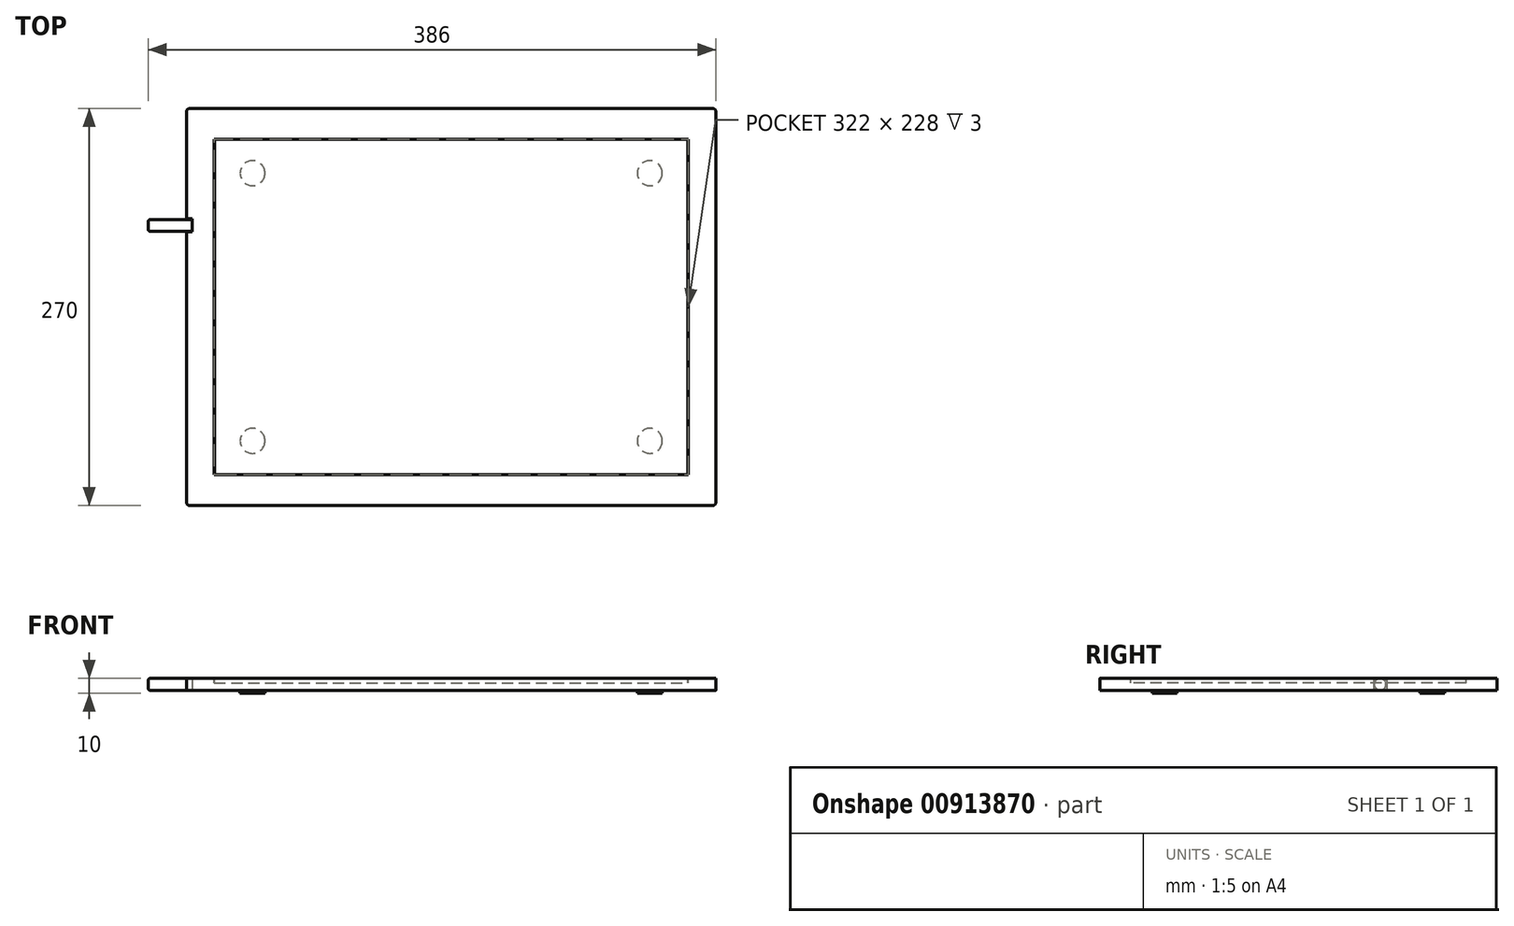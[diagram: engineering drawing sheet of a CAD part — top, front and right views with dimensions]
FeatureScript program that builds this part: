
annotation { "Feature Type Name" : "Feature", "Feature Type Description" : "" }
export const myFeature = defineFeature(function(context is Context, id is Id, definition is map)
    precondition{}
    {
        {
            var Q0;
            Q0=qCreatedBy(makeId("Top.planeOp"),FACE);
            var sketch = newSketch(context, id + "F0", { "sketchPlane" : qUnion([Q0])});
            skLineSegment(sketch, "E0.bottom", {"start": v(0, 0) * mm, "end": v(360, 0) * mm});
            skLineSegment(sketch, "E0.top", {"start": v(0, -270) * mm, "end": v(360, -270) * mm});
            skLineSegment(sketch, "E0.left", {"start": v(0, 0) * mm, "end": v(0, -270) * mm});
            skLineSegment(sketch, "E0.right", {"start": v(360, 0) * mm, "end": v(360, -270) * mm});
            skSolve(sketch);
        }
        {
            var Q0;
            Q0 = qSketchRegion(id + "F0", true);
            extrude(context, id + "F1", {"entities" : qUnion([Q0]), "depth" : 8 * mm, "offsetDistance" : 25 * mm});
        }
        {
            var Q0;
            Q0=makeQuery(id+"F1.opExtrude","CAP_FACE",FACE,{"disambiguationData":[OSD([sQuery(id+"F0.wireOp",EDGE,"E0.bottom"),sQuery(id+"F0.wireOp",EDGE,"E0.top"),sQuery(id+"F0.wireOp",EDGE,"E0.left"),sQuery(id+"F0.wireOp",EDGE,"E0.right")])],"isStart":true});
            var sketch = newSketch(context, id + "F2", { "sketchPlane" : qUnion([Q0])});
            skLineSegment(sketch, "E1", {"start": v(180, 270) * mm, "end": v(180, 0) * mm, "construction": true});
            skLineSegment(sketch, "E2", {"start": v(0, 135) * mm, "end": v(360, 135) * mm, "construction": true});
            skCircle(sketch, "E3", {"center": v(45, 44) * mm, "radius": 8.5 * mm});
            skCircle(sketch, "E4.MirrorC", {"center": v(315, 44) * mm, "radius": 8.5 * mm});
            skCircle(sketch, "E5.MirrorC", {"center": v(45, 226) * mm, "radius": 8.5 * mm});
            skCircle(sketch, "E6.MirrorC", {"center": v(315, 226) * mm, "radius": 8.5 * mm});
            skSolve(sketch);
        }
        {
            var Q0;
            Q0 = qSketchRegion(id + "F2", true);
            extrude(context, id + "F3", {"entities" : qUnion([Q0]), "operationType" : NewBodyOperationType.ADD, "depth" : 2 * mm, "offsetDistance" : 25 * mm});
        }
        {
            var Q0;
            Q0=makeQuery(id+"F1.opExtrude","CAP_FACE",FACE,{"disambiguationData":[OSD([sQuery(id+"F0.wireOp",EDGE,"E0.bottom"),sQuery(id+"F0.wireOp",EDGE,"E0.top"),sQuery(id+"F0.wireOp",EDGE,"E0.left"),sQuery(id+"F0.wireOp",EDGE,"E0.right")])],"isStart":true});
            var sketch = newSketch(context, id + "F4", { "sketchPlane" : qUnion([Q0])});
            skLineSegment(sketch, "E7.bottom", {"start": v(0, 84) * mm, "end": v(4, 84) * mm});
            skLineSegment(sketch, "E7.top", {"start": v(0, 75) * mm, "end": v(4, 75) * mm});
            skLineSegment(sketch, "E7.left", {"start": v(0, 84) * mm, "end": v(0, 75) * mm});
            skLineSegment(sketch, "E7.right", {"start": v(4, 84) * mm, "end": v(4, 75) * mm});
            skSolve(sketch);
        }
        {
            var Q0;
            Q0 = qSketchRegion(id + "F4", true);
            extrude(context, id + "F5", {"entities" : qUnion([Q0]), "operationType" : NewBodyOperationType.REMOVE, "endBound" : BoundingType.THROUGH_ALL, "oppositeDirection" : true, "depth" : 25 * mm, "offsetDistance" : 25 * mm});
        }
        {
            var Q0;
            Q0=makeQuery(id+"F1.opExtrude","SWEPT_EDGE",EDGE,{"disambiguationData":[OSD([sQuery(id+"F0.wireOp",EDGE,"E0.top"),sQuery(id+"F0.wireOp",EDGE,"E0.left")])]});
            var Q1;
            Q1=makeQuery(id+"F1.opExtrude","SWEPT_EDGE",EDGE,{"disambiguationData":[OSD([sQuery(id+"F0.wireOp",EDGE,"E0.top"),sQuery(id+"F0.wireOp",EDGE,"E0.right")])]});
            var Q2;
            Q2=makeQuery(id+"F1.opExtrude","SWEPT_EDGE",EDGE,{"disambiguationData":[OSD([sQuery(id+"F0.wireOp",EDGE,"E0.bottom"),sQuery(id+"F0.wireOp",EDGE,"E0.left")])]});
            var Q3;
            Q3=makeQuery(id+"F1.opExtrude","SWEPT_EDGE",EDGE,{"disambiguationData":[OSD([sQuery(id+"F0.wireOp",EDGE,"E0.bottom"),sQuery(id+"F0.wireOp",EDGE,"E0.right")])]});
            var Q4;
            Q4=makeQuery(id+"F5.boolean.opBoolean","COPY",EDGE,{"derivedFrom":makeQuery(id+"F5.opExtrude","SWEPT_EDGE",EDGE,{"disambiguationData":[OSD([sQuery(id+"F0.wireOp",EDGE,"E0.left"),sQuery(id+"F4.wireOp",EDGE,"E7.bottom"),sQuery(id+"F4.wireOp",EDGE,"E7.left")])]})});
            var Q5;
            Q5=makeQuery(id+"F5.boolean.opBoolean","COPY",EDGE,{"derivedFrom":makeQuery(id+"F5.opExtrude","SWEPT_EDGE",EDGE,{"disambiguationData":[OSD([sQuery(id+"F0.wireOp",EDGE,"E0.left"),sQuery(id+"F4.wireOp",EDGE,"E7.top"),sQuery(id+"F4.wireOp",EDGE,"E7.left")])]})});
            fillet(context, id + "F6", {"entities" : qUnion([Q0, Q1, Q2, Q3, Q4, Q5]), "tangentPropagation" : true, "radius" : 2.5 * mm, "defaultsChanged" : false, "vertexSettings" : [], "allowEdgeOverflow" : false});
        }
        {
            var Q0;
            Q0=makeQuery(id+"F5.boolean.opBoolean","COPY",FACE,{"derivedFrom":makeQuery(id+"F5.opExtrude","SWEPT_FACE",FACE,{"disambiguationData":[OSD([sQuery(id+"F4.wireOp",EDGE,"E7.right")])]})});
            var sketch = newSketch(context, id + "F7", { "sketchPlane" : qUnion([Q0])});
            skCircle(sketch, "E8", {"center": v(79.5, 4) * mm, "radius": 4 * mm});
            skSolve(sketch);
        }
        {
            var Q0;
            Q0 = qSketchRegion(id + "F7", true);
            extrude(context, id + "F8", {"entities" : qUnion([Q0]), "operationType" : NewBodyOperationType.ADD, "depth" : 30 * mm, "offsetDistance" : 25 * mm});
        }
        {
            var Q0;
            Q0=makeQuery(id+"F8.opExtrude","CAP_EDGE",EDGE,{"disambiguationData":[OSD([sQuery(id+"F7.wireOp",EDGE,"E8")])],"isStart":false});
            fillet(context, id + "F9", {"entities" : qUnion([Q0]), "tangentPropagation" : true, "crossSection" : FilletCrossSection.CURVATURE, "radius" : 1 * mm, "magnitude" : 0.1, "defaultsChanged" : true, "vertexSettings" : []});
        }
        {
            var Q0;
            Q0=makeQuery(id+"F1.opExtrude","CAP_FACE",FACE,{"disambiguationData":[OSD([sQuery(id+"F0.wireOp",EDGE,"E0.bottom"),sQuery(id+"F0.wireOp",EDGE,"E0.top"),sQuery(id+"F0.wireOp",EDGE,"E0.left"),sQuery(id+"F0.wireOp",EDGE,"E0.right")])],"isStart":false});
            var sketch = newSketch(context, id + "F10", { "sketchPlane" : qUnion([Q0])});
            skLineSegment(sketch, "E9.bottom", {"start": v(19, -21) * mm, "end": v(341, -21) * mm});
            skLineSegment(sketch, "E9.top", {"start": v(19, -249) * mm, "end": v(341, -249) * mm});
            skLineSegment(sketch, "E9.left", {"start": v(19, -21) * mm, "end": v(19, -249) * mm});
            skLineSegment(sketch, "E9.right", {"start": v(341, -21) * mm, "end": v(341, -249) * mm});
            skSolve(sketch);
        }
        {
            var Q0;
            Q0 = qSketchRegion(id + "F10", true);
            extrude(context, id + "F11", {"entities" : qUnion([Q0]), "operationType" : NewBodyOperationType.REMOVE, "oppositeDirection" : true, "depth" : 3 * mm, "offsetDistance" : 25 * mm});
        }
        {
            var Q0;
            Q0=makeQuery(id+"F1.opExtrude","CAP_FACE",FACE,{"disambiguationData":[OSD([sQuery(id+"F0.wireOp",EDGE,"E0.bottom"),sQuery(id+"F0.wireOp",EDGE,"E0.top"),sQuery(id+"F0.wireOp",EDGE,"E0.left"),sQuery(id+"F0.wireOp",EDGE,"E0.right")])],"isStart":false});
            var sketch = newSketch(context, id + "F12", { "sketchPlane" : qUnion([Q0])});
            skLineSegment(sketch, "E10.bottom", {"start": v(19.1, -21.1) * mm, "end": v(340.9, -21.1) * mm});
            skLineSegment(sketch, "E10.top", {"start": v(19.1, -248.9) * mm, "end": v(340.9, -248.9) * mm});
            skLineSegment(sketch, "E10.left", {"start": v(19.1, -21.1) * mm, "end": v(19.1, -248.9) * mm});
            skLineSegment(sketch, "E10.right", {"start": v(340.9, -21.1) * mm, "end": v(340.9, -248.9) * mm});
            skSolve(sketch);
        }
        {
            var Q0;
            Q0 = qSketchRegion(id + "F12", true);
            extrude(context, id + "F13", {"entities" : qUnion([Q0]), "oppositeDirection" : true, "depth" : 3 * mm, "offsetDistance" : 25 * mm});
        }
    });
